# Revit family: RBA2732-UG-Series
name_source: partatom
category: Plumbing Fixtures
units: mm (PartAtom-declared; Revit-internal decimal feet)

## family parameters
Always vertical = Yes
Cut with Voids When Loaded = No
Part Type = Normal
Room Calculation Point = No
Round Connector Dimension = Use Diameter
Shared = Yes
Work Plane-Based = No

## types (3) — shared parameters
CW Connection = Yes
HW Connection = Yes
Manufacturer = RBA Group
Materials and Finishes = #304 Stainless Steel, Satin Finish
Modified Issue = 20220815.01
URL = https://www.rba.com.au
Vent Connection = Yes
Waste Connection = Yes
zero-valued in all types: Default Elevation

## per-type parameters (varying)
| type | Description | Flexi Bubbler | Glass Filler | Stainless Bubbler |
| RBA2732-032-UG | Wall mounted ‘Compact’ satin finish water cooler, w/ flexible bubbler, 30L/hr | Yes | No | No |
| RBA2732-033-UG | Wall mounted ‘Compact’ satin finish water cooler, w/ stainless bubbler, 30L/hr | No | No | Yes |
| RBA2732-132-UG | Wall mounted ‘Compact’ satin finish water cooler, w/ flexible bubbler and glass filler, 30L/hr | Yes | Yes | No |

note: column(s) folded — value = type name in every type: Model

## geometry (parser evidence)
native form markers: Blend x4, Sweep x4
no freeform markers — native parametric forms only
